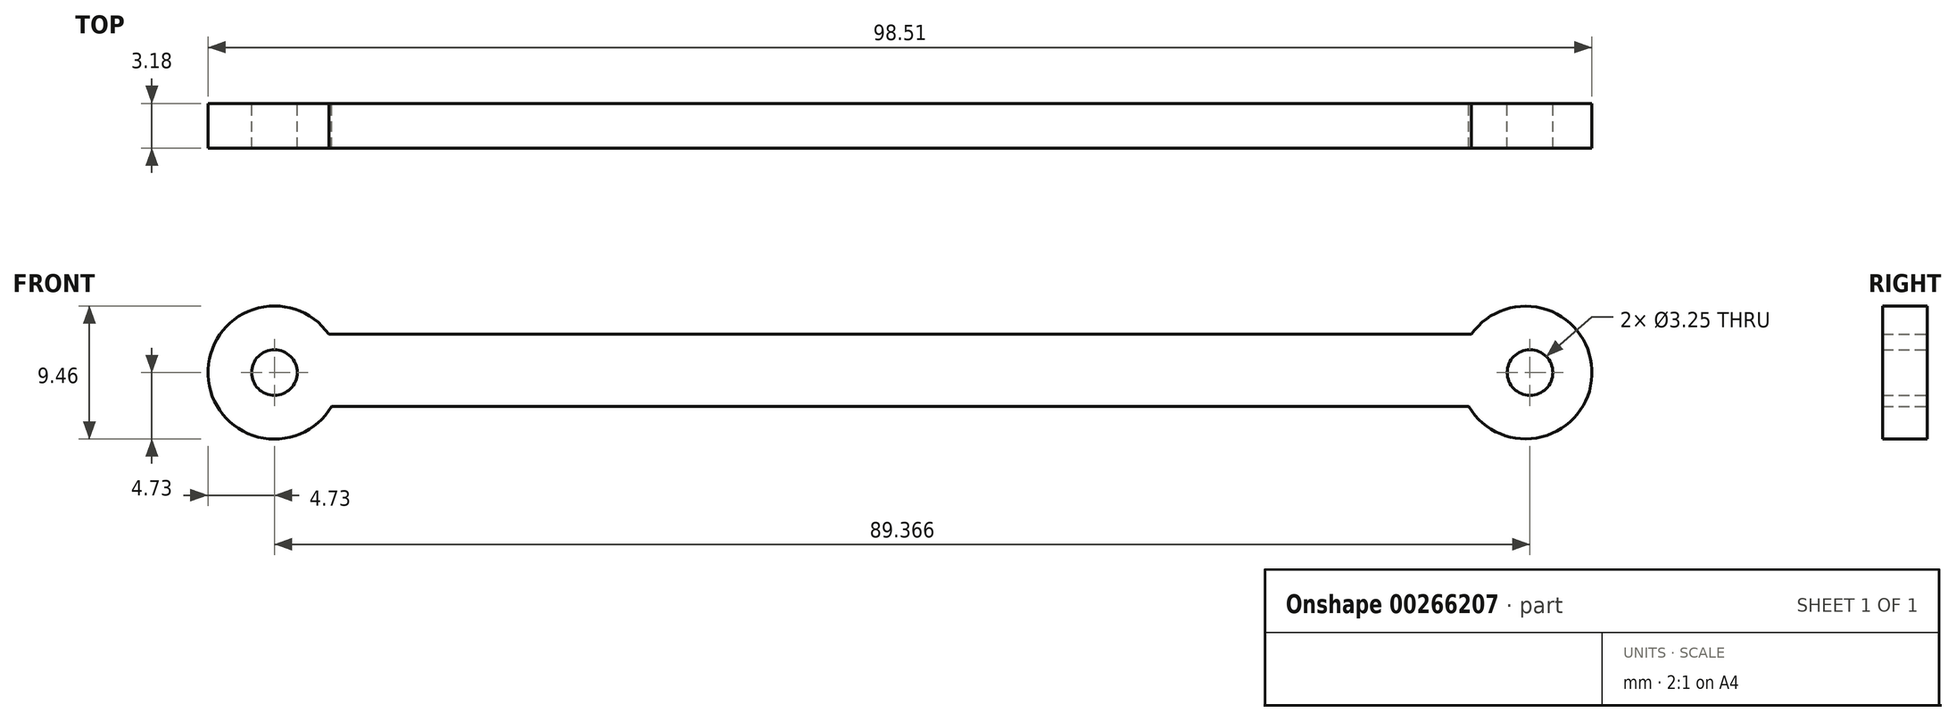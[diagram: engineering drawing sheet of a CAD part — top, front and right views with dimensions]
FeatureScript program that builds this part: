
annotation { "Feature Type Name" : "Feature", "Feature Type Description" : "" }
export const myFeature = defineFeature(function(context is Context, id is Id, definition is map)
    precondition{}
    {
        {
            var Q0;
            Q0=qCreatedBy(makeId("Front.planeOp"),FACE);
            var sketch = newSketch(context, id + "F0", { "sketchPlane" : qUnion([Q0])});
            skCircle(sketch, "E0", {"center": v(0, 0) * mm, "radius": 4.73 * mm});
            skLineSegment(sketch, "E1", {"start": v(0, 2.72) * mm, "end": v(89.06, 2.72) * mm});
            skLineSegment(sketch, "E2", {"start": v(0, -2.41) * mm, "end": v(89.06, -2.41) * mm});
            skCircle(sketch, "E3", {"center": v(89.06, 0) * mm, "radius": 4.72 * mm});
            skSolve(sketch);
        }
        {
            var Q0;
            Q0 = qSketchRegion(id + "F0", true);
            extrude(context, id + "F1", {"entities" : qUnion([Q0]), "depth" : 3.17 * mm});
        }
        {
            var Q0;
            Q0=qCreatedBy(makeId("Front.planeOp"),FACE);
            var sketch = newSketch(context, id + "F2", { "sketchPlane" : qUnion([Q0])});
            skPoint(sketch, "E4", {"position": v(0, 0) * mm});
            skPoint(sketch, "E5", {"position": v(89.37, 0) * mm});
            skSolve(sketch);
        }
        {
            var Q0;
            Q0=sQuery(id+"F2.wireOp",VERTEX,"E4");
            var Q1;
            Q1=sQuery(id+"F2.wireOp",VERTEX,"E5");
            var Q2;
            Q2=makeQuery(id+"F1.opExtrude","SWEPT_BODY",BODY,{"disambiguationData":[OSD([sQuery(id+"F0.wireOp",EDGE,"E0"),sQuery(id+"F0.wireOp",EDGE,"E1"),sQuery(id+"F0.wireOp",EDGE,"E2"),sQuery(id+"F0.wireOp",EDGE,"E3")])]});
            hole(context, id + "F3", {"style" : HoleStyle.SIMPLE, "endStyle" : HoleEndStyle.THROUGH, "oppositeDirection" : true, "holeDiameter" : 3.25 * mm, "tappedDepth" : 12.7 * mm, "tapClearance" : 3, "locations" : qUnion([Q0, Q1]), "scope" : qUnion([Q2])});
        }
    });
